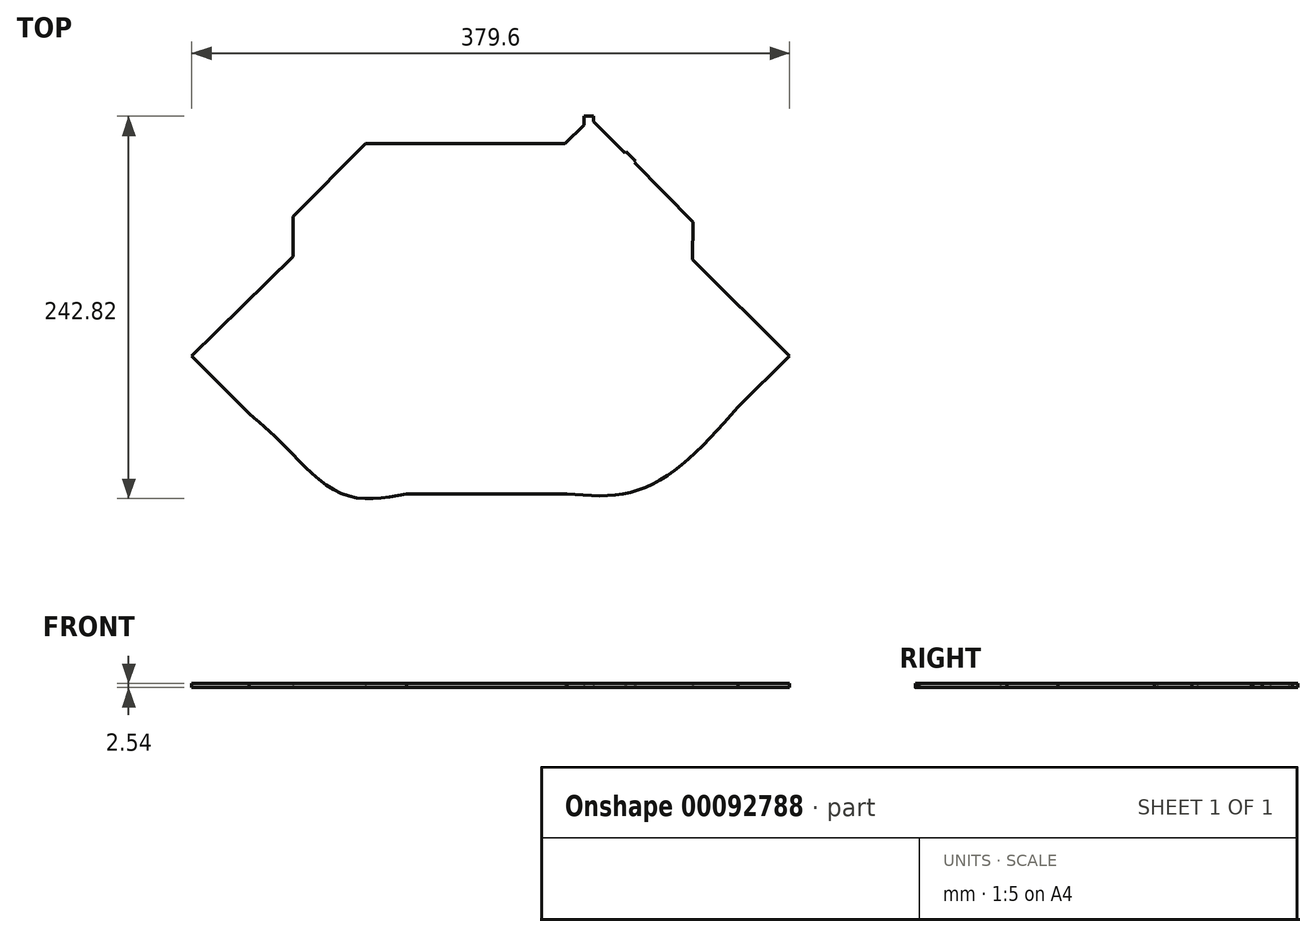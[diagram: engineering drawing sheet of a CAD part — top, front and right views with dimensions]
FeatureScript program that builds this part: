
annotation { "Feature Type Name" : "Feature", "Feature Type Description" : "" }
export const myFeature = defineFeature(function(context is Context, id is Id, definition is map)
    precondition{}
    {
        {
            var Q0;
            Q0=qCreatedBy(makeId("Top.planeOp"),FACE);
            var sketch = newSketch(context, id + "F0", { "sketchPlane" : qUnion([Q0])});
            skFitSpline(sketch, "E0", {"points": [v(157.08, -64.8) * mm, v(117.69, -104.35) * mm, v(84.4, -119.84) * mm, v(48.48, -119.87) * mm]});
            skLineSegment(sketch, "E1", {"start": v(-189.8, -32.17) * mm, "end": v(-125.58, 30.86) * mm});
            skLineSegment(sketch, "E2", {"start": v(-125.58, 30.86) * mm, "end": v(-125.58, 56.27) * mm});
            skLineSegment(sketch, "E3", {"start": v(-125.58, 56.27) * mm, "end": v(-79.33, 102.59) * mm});
            skLineSegment(sketch, "E4", {"start": v(-79.33, 102.59) * mm, "end": v(47.41, 102.59) * mm});
            skLineSegment(sketch, "E5", {"start": v(47.41, 102.59) * mm, "end": v(59.3, 114.48) * mm});
            skLineSegment(sketch, "E6", {"start": v(59.3, 114.48) * mm, "end": v(59.3, 119.97) * mm});
            skLineSegment(sketch, "E7", {"start": v(59.3, 119.97) * mm, "end": v(65.48, 119.97) * mm});
            skLineSegment(sketch, "E8", {"start": v(65.48, 119.97) * mm, "end": v(65.48, 116.5) * mm});
            skLineSegment(sketch, "E9", {"start": v(65.48, 116.5) * mm, "end": v(85.26, 96.73) * mm});
            skLineSegment(sketch, "E10", {"start": v(85.26, 96.73) * mm, "end": v(86.04, 97.52) * mm});
            skLineSegment(sketch, "E11", {"start": v(86.04, 97.52) * mm, "end": v(92.15, 91.4) * mm});
            skLineSegment(sketch, "E12", {"start": v(92.15, 91.4) * mm, "end": v(91.4, 90.66) * mm});
            skLineSegment(sketch, "E13", {"start": v(91.4, 90.66) * mm, "end": v(128.5, 52.92) * mm});
            skLineSegment(sketch, "E14", {"start": v(128.5, 52.92) * mm, "end": v(128.14, 28.91) * mm});
            skLineSegment(sketch, "E15", {"start": v(128.14, 28.91) * mm, "end": v(189.8, -32.32) * mm});
            skLineSegment(sketch, "E16", {"start": v(189.8, -32.32) * mm, "end": v(157.08, -64.8) * mm});
            skFitSpline(sketch, "E17", {"points": [v(-53.42, -119.97) * mm, v(-93.73, -120) * mm, v(-130.17, -90.05) * mm, v(-153.42, -68.7) * mm]});
            skLineSegment(sketch, "E18", {"start": v(48.48, -119.87) * mm, "end": v(-53.42, -119.97) * mm});
            skLineSegment(sketch, "E19", {"start": v(-153.42, -68.7) * mm, "end": v(-189.8, -32.17) * mm});
            skSolve(sketch);
        }
        {
            var Q0;
            Q0=makeQuery(id+"F0.imprint","IMPRINT",FACE,{"disambiguationData":[TD([[makeQuery(id+"F0.imprint","IMPRINT",EDGE,{"derivedFrom":sQuery(id+"F0.wireOp",EDGE,"E0")}),-1.0]])]});
            extrude(context, id + "F1", {"entities" : qUnion([Q0]), "depth" : 2.54 * mm});
        }
    });
